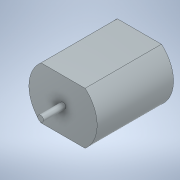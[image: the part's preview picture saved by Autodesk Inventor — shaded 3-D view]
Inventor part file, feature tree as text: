
AUTODESK INVENTOR PART (.ipt)
format: ipt  version: 2020 (Build 240168000, 168)  size: 106,496 bytes
history: native  units: mm
features: extrude x2, sketch x2
ambient origin geometry x8: Origin, YZ Plane, XZ Plane, XY Plane, X Axis, Y Axis, Z Axis, Center Point
bodies: Solid1 (feature_tree)
feature tree (4):
  extrude  "Extrusion1"  Depth=26.9mm
  extrude  "Extrusion2"  Depth=18.3mm
  sketch  "Sketch1"  dims[d0=17.3mm d2=26.9mm d3=0.0mm d4=2.0mm]
  sketch  "Sketch2"  dims[d5=7.9mm d6=0.0mm d7=24.0mm d8=18.3mm]
